# Revit family: Domotics-DomesticRanges-GEWISS-CHORUS_POWER-SOCKET-OUTLET_EURUSA
name_source: partatom
category: Apparecchi elettrici
revit_build: Autodesk Revit 2016 (Build: 20161004_0715(x64)
units: mm (PartAtom-declared; Revit-internal decimal feet)

## family parameters
Condiviso = Sì
Host = Superficie
Mantenere orientamento annotazione = Sì
Punto di calcolo locali = Sì
Quota connettore circolare = Usa diametro
Taglio con vuoti quando caricato = Sì
Tipo di parte = Normale

## types (6) — shared parameters
Breaking capacity: = 1.25 In (100 position changes)
Carico apparente = 0 VA
Catalogue = DOMOTICS
Catalogue Range = CHORUS - DOMESTIC RANGE
Category = Socket-outlet
Description. = Socket-outlet
Electrocod = 0131
For plug pins = Ã˜ 4 mm Flat
Glow Wire Test = 850°C
IDF = fd8d0965-b28c-4179-a336-df09c3b4294f
IDT = 613f9da3-ec27-4742-84bd-e3589e01972c
Immagine tipo = GW14288.jpg
Insulation resistance = > 5 MOhm
N. poli = 1
No. Chorus modules = 1
No. Chorus modules: = 1
Produttore = GEWISS S.p.A.
Prolonged operation (no.of position changes) = 10.000 at In 250 V ac cosÃ˜=0,8
Prospetto di default = 1219 mm
Resistance at test voltage = 2000 V at 50 Hz for 1 minute
SEO = Socket outlet
Standard = USA
Standard: = Euro-American
Standard; = IEC 60884-1
TXT ELETTRICO = 15
Technical sheet = https://www.gewiss.com
Terminal grip on cable traction = > 50 N
Terminal tightening capacity flexible cables (mm2) = min. 0,75 - max. 2x4
Terminal tightening capacity rigid cables (mm2) = min. 0,5 - max. 2x2,5
Thermo-pressure with ball = 125
Tipo = Chorus Prese EuroUsa_GENERICO : GW14288 Presa 2P+T standard Euroamericano titanio
URL = https://www.gewiss.com
Version file RFA = 19.0
Volt = 230 V
Voltage = 250/125V AC
Voltage: = 250/125V AC
Wiring terminals = With screw

## per-type parameters (varying)
| type | Colour | Description: | Descrizione | EAN code | Modello |
| GW14288 - Socket outlet 1M 2P+E 15A usa st titanium | Titanium | 2P+E - 15A | SOCKET 1M 2P+E 15A USA ST TITANIUM | 8011564439443 | GW14288 |
| GW12288 - Socket outlet 1M 2P+E 15A usa st black | Black | 2P+E - 15A | SOCKET 1M 2P+E 15A USA ST BLACK | 8011564439436 | GW12288 |
| GW10288 - Socket outlet 1M 2P+E 15A usa white | White | 2P+E - 15A | S. OUTLET 1M 2P+E 15A USA WHITE | 8011564439429 | GW10288 |
| GW12287 - Socket outlet 1M 2P 15A eu/usa st black | Black | 2P - 15A | SOCKET 1M 2P 15A EU/USA ST BLACK | 8011564267183 | GW12287 |
| GW14287 - Socket outlet 1M 2P 15A eu/usa st titanium | Titanium | 2P - 15A | SOCKET 1M 2P 15A EU/USA ST TITANIUM | 8011564266421 | GW14287 |
| GW10287 - Socket outlet 1M 2P 15A eu/usa white | White | 2P - 15A | S. OUTLET 1M 2P 15A EU/USA WHITE | 8011564258266 | GW10287 |

note: source unit labels omitted for Thermo-pressure with ball — the stored unit's dimension contradicts the parameter name (converter mislabeling)

## geometry (parser evidence)
native form markers: Sweep x1
no freeform markers — native parametric forms only
